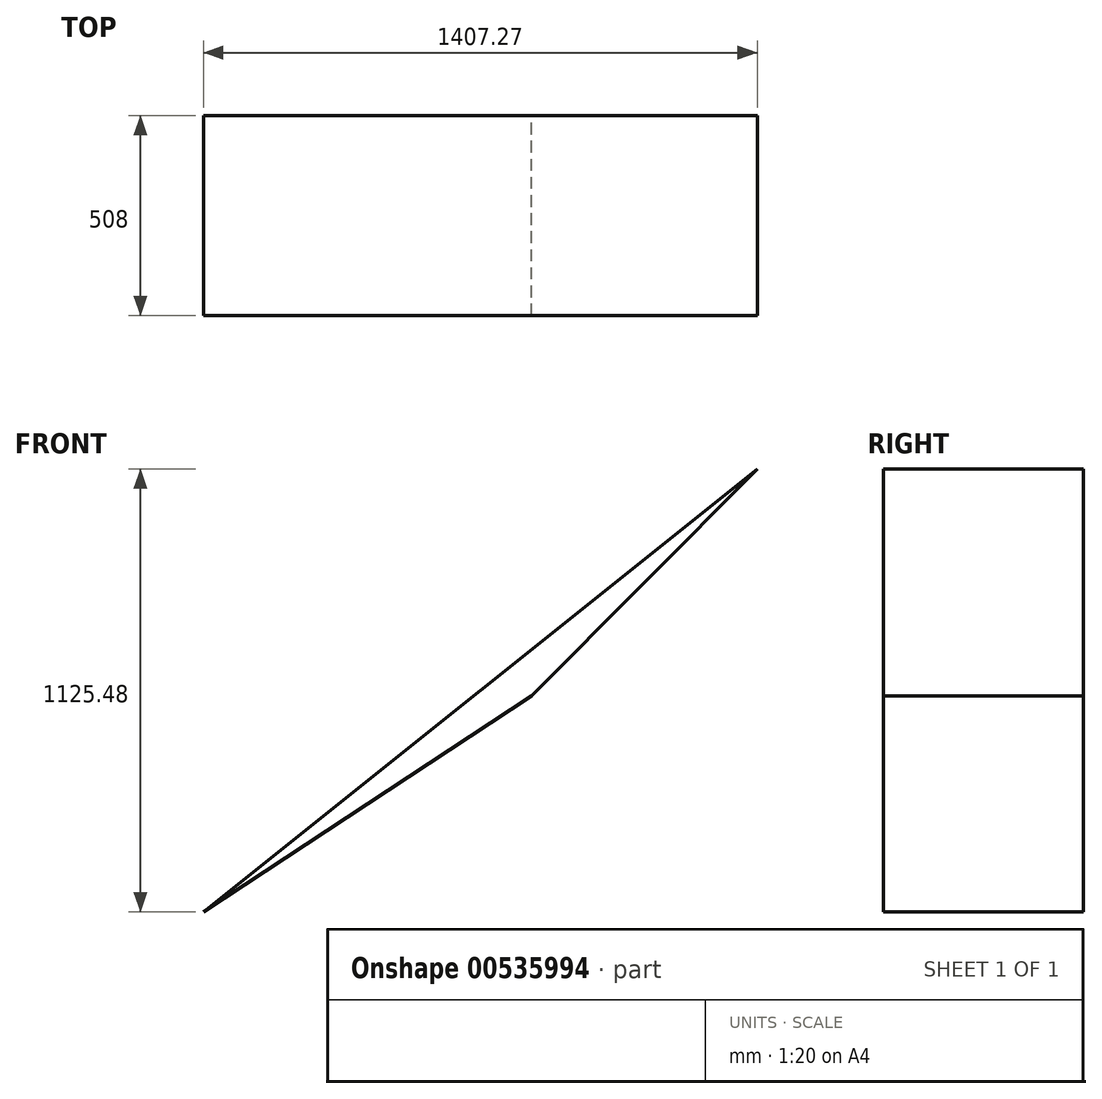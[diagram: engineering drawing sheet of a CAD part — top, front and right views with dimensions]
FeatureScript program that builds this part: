
annotation { "Feature Type Name" : "Feature", "Feature Type Description" : "" }
export const myFeature = defineFeature(function(context is Context, id is Id, definition is map)
    precondition{}
    {
        {
            var Q0;
            Q0=qCreatedBy(makeId("Front.planeOp"),FACE);
            var sketch = newSketch(context, id + "F0", { "sketchPlane" : qUnion([Q0])});
            skLineSegment(sketch, "E0", {"start": v(-1562.96, -1286.83) * mm, "end": v(-1562.96, -1286.83) * mm});
            skLineSegment(sketch, "E1", {"start": v(-1562.96, -1286.83) * mm, "end": v(-729.6, -737.82) * mm});
            skLineSegment(sketch, "E2", {"start": v(-729.6, -737.82) * mm, "end": v(-155.7, -161.35) * mm});
            skLineSegment(sketch, "E3", {"start": v(-155.7, -161.35) * mm, "end": v(-1562.96, -1286.83) * mm});
            skSolve(sketch);
        }
        {
            var Q0;
            Q0 = qSketchRegion(id + "F0", true);
            extrude(context, id + "F1", {"bodyType" : ToolBodyType.SURFACE, "surfaceEntities" : qUnion([Q0]), "depth" : 508 * mm, "offsetDistance" : 25.4 * mm});
        }
    });
